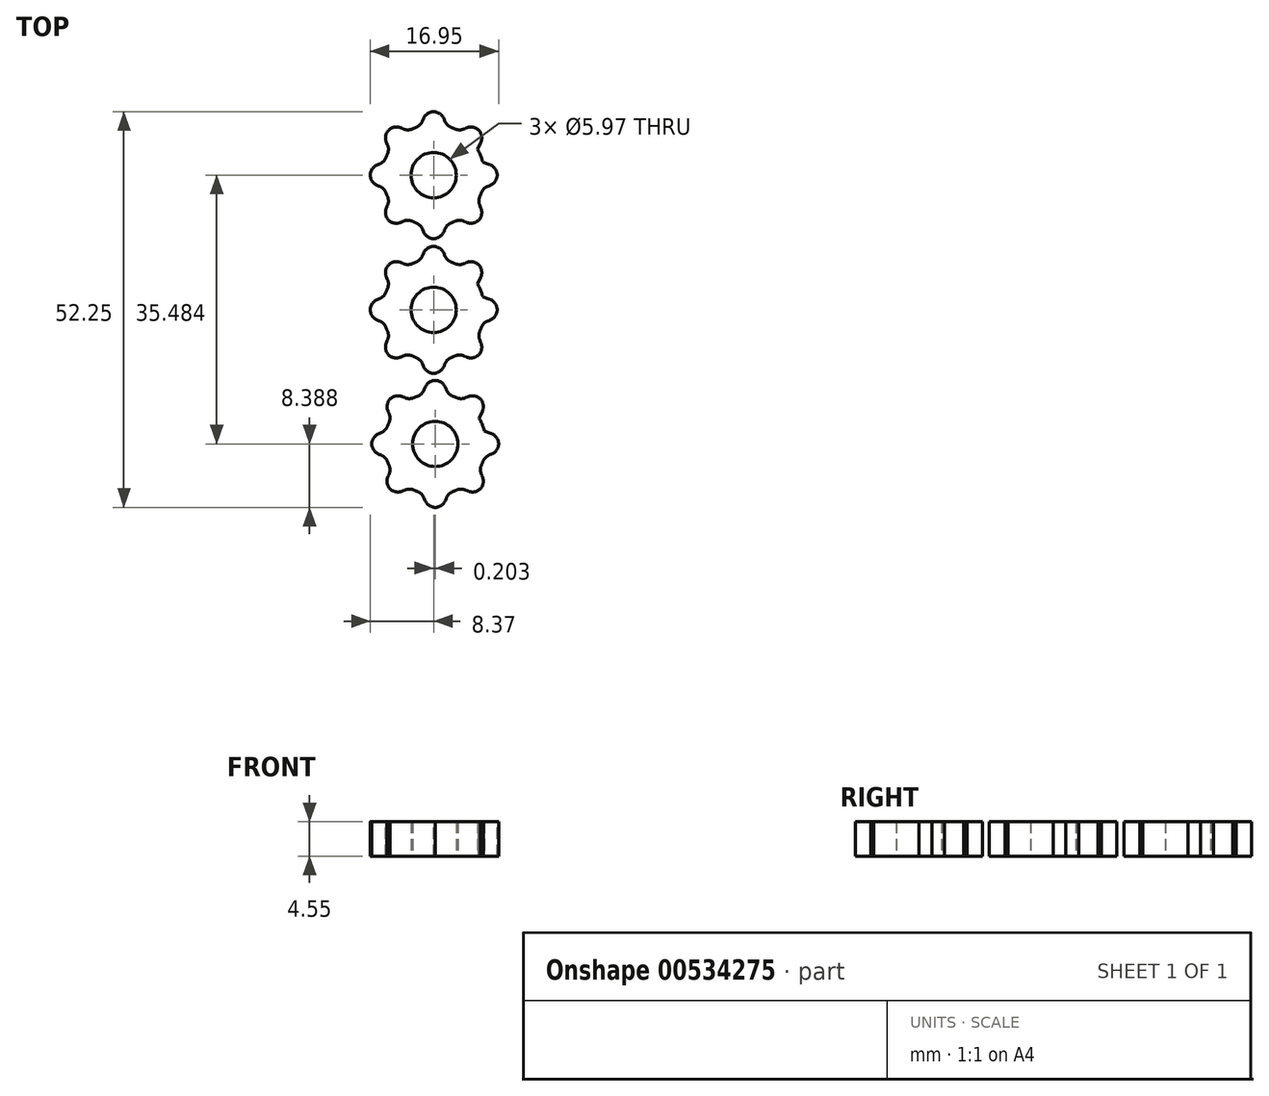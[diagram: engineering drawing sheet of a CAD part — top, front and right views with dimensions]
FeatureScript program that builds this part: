
annotation { "Feature Type Name" : "Feature", "Feature Type Description" : "" }
export const myFeature = defineFeature(function(context is Context, id is Id, definition is map)
    precondition{}
    {
        {
            var Q0;
            Q0=qCreatedBy(makeId("Top.planeOp"),FACE);
            var sketch = newSketch(context, id + "F0", { "sketchPlane" : qUnion([Q0])});
            skCircle(sketch, "E0", {"center": v(-14.29, 61.74) * mm, "radius": 6.71 * mm});
            skLineSegment(sketch, "E1", {"start": v(-22.66, 62.77) * mm, "end": v(-22.66, 60.71) * mm});
            skLineSegment(sketch, "E2", {"start": v(-22.66, 62.77) * mm, "end": v(-20.78, 63.44) * mm});
            skLineSegment(sketch, "E3", {"start": v(-22.66, 60.71) * mm, "end": v(-20.78, 60.04) * mm});
            skLineSegment(sketch, "E4", {"start": v(-19.52, 68.4) * mm, "end": v(-20.95, 66.97) * mm});
            skLineSegment(sketch, "E5", {"start": v(-20.95, 66.97) * mm, "end": v(-20.08, 65.13) * mm});
            skLineSegment(sketch, "E6", {"start": v(-19.52, 68.4) * mm, "end": v(-17.68, 67.54) * mm});
            skLineSegment(sketch, "E7", {"start": v(-15.31, 70.12) * mm, "end": v(-13.27, 70.12) * mm});
            skLineSegment(sketch, "E8", {"start": v(-13.27, 70.12) * mm, "end": v(-12.59, 68.24) * mm});
            skLineSegment(sketch, "E9", {"start": v(-15.31, 70.12) * mm, "end": v(-16, 68.24) * mm});
            skLineSegment(sketch, "E10", {"start": v(-10.9, 67.54) * mm, "end": v(-9.06, 68.4) * mm});
            skLineSegment(sketch, "E11", {"start": v(-9.06, 68.4) * mm, "end": v(-7.63, 66.97) * mm});
            skLineSegment(sketch, "E12", {"start": v(-7.63, 66.97) * mm, "end": v(-8.5, 65.13) * mm});
            skLineSegment(sketch, "E13", {"start": v(-5.9, 62.77) * mm, "end": v(-5.9, 60.72) * mm});
            skLineSegment(sketch, "E14", {"start": v(-5.9, 60.72) * mm, "end": v(-7.8, 60.04) * mm});
            skLineSegment(sketch, "E15", {"start": v(-5.9, 62.77) * mm, "end": v(-7.8, 63.44) * mm});
            skLineSegment(sketch, "E16", {"start": v(-7.63, 56.51) * mm, "end": v(-9.06, 55.08) * mm});
            skLineSegment(sketch, "E17", {"start": v(-9.06, 55.08) * mm, "end": v(-10.9, 55.95) * mm});
            skLineSegment(sketch, "E18", {"start": v(-7.63, 56.51) * mm, "end": v(-8.5, 58.35) * mm});
            skLineSegment(sketch, "E19", {"start": v(-13.27, 53.35) * mm, "end": v(-15.31, 53.35) * mm});
            skLineSegment(sketch, "E20", {"start": v(-15.31, 53.35) * mm, "end": v(-16, 55.25) * mm});
            skLineSegment(sketch, "E21", {"start": v(-13.27, 53.35) * mm, "end": v(-12.59, 55.25) * mm});
            skLineSegment(sketch, "E22", {"start": v(-20.96, 56.5) * mm, "end": v(-19.53, 55.07) * mm});
            skLineSegment(sketch, "E23", {"start": v(-19.53, 55.07) * mm, "end": v(-17.68, 55.95) * mm});
            skLineSegment(sketch, "E24", {"start": v(-20.96, 56.5) * mm, "end": v(-20.08, 58.35) * mm});
            skCircle(sketch, "E25", {"center": v(-14.29, 61.74) * mm, "radius": 2.99 * mm});
            skSolve(sketch);
        }
        {
            var Q0;
            Q0=makeQuery(id+"F0.imprint","IMPRINT",FACE,{"disambiguationData":[TD([[makeQuery(id+"F0.imprint","IMPRINT",EDGE,{"derivedFrom":sQuery(id+"F0.wireOp",EDGE,"E25")}),-1.0]])]});
            extrude(context, id + "F1", {"entities" : qUnion([Q0]), "depth" : 4.55 * mm, "offsetDistance" : 25.4 * mm});
        }
        {
            var Q0;
            Q0=makeQuery(id+"F0.imprint","IMPRINT",FACE,{"disambiguationData":[TD([[makeQuery(id+"F0.imprint","IMPRINT",EDGE,{"derivedFrom":sQuery(id+"F0.wireOp",EDGE,"E1")}),1.0]])]});
            var Q1;
            Q1=makeQuery(id+"F0.imprint","IMPRINT",FACE,{"disambiguationData":[TD([[makeQuery(id+"F0.imprint","IMPRINT",EDGE,{"derivedFrom":sQuery(id+"F0.wireOp",EDGE,"E7")}),-1.0]])]});
            var Q2;
            Q2=makeQuery(id+"F0.imprint","IMPRINT",FACE,{"disambiguationData":[TD([[makeQuery(id+"F0.imprint","IMPRINT",EDGE,{"derivedFrom":sQuery(id+"F0.wireOp",EDGE,"E4")}),1.0]])]});
            var Q3;
            {var subQ0=sQuery(id+"F0.wireOp",EDGE,"E10");Q3=makeQuery(id+"F0.imprint","IMPRINT",FACE,{"disambiguationData":[TD([[makeQuery(id+"F0.imprint","IMPRINT",EDGE,{"derivedFrom":subQ0}),-1.0]])]});}
            var Q4;
            Q4=makeQuery(id+"F0.imprint","IMPRINT",FACE,{"disambiguationData":[TD([[makeQuery(id+"F0.imprint","IMPRINT",EDGE,{"derivedFrom":sQuery(id+"F0.wireOp",EDGE,"E13")}),-1.0]])]});
            var Q5;
            Q5=makeQuery(id+"F0.imprint","IMPRINT",FACE,{"disambiguationData":[TD([[makeQuery(id+"F0.imprint","IMPRINT",EDGE,{"derivedFrom":sQuery(id+"F0.wireOp",EDGE,"E16")}),-1.0]])]});
            var Q6;
            Q6=makeQuery(id+"F0.imprint","IMPRINT",FACE,{"disambiguationData":[TD([[makeQuery(id+"F0.imprint","IMPRINT",EDGE,{"derivedFrom":sQuery(id+"F0.wireOp",EDGE,"E19")}),-1.0]])]});
            var Q7;
            Q7=makeQuery(id+"F0.imprint","IMPRINT",FACE,{"disambiguationData":[TD([[makeQuery(id+"F0.imprint","IMPRINT",EDGE,{"derivedFrom":sQuery(id+"F0.wireOp",EDGE,"E22")}),1.0]])]});
            extrude(context, id + "F2", {"entities" : qUnion([Q0, Q1, Q2, Q3, Q4, Q5, Q6, Q7]), "operationType" : NewBodyOperationType.ADD, "depth" : 4.55 * mm, "offsetDistance" : 25.4 * mm});
        }
        {
            var Q0;
            Q0=makeQuery(id+"F2.opExtrude","SWEPT_EDGE",EDGE,{"disambiguationData":[OSD([sQuery(id+"F0.wireOp",EDGE,"E13"),sQuery(id+"F0.wireOp",EDGE,"E15")])]});
            var Q1;
            Q1=makeQuery(id+"F2.opExtrude","SWEPT_EDGE",EDGE,{"disambiguationData":[OSD([sQuery(id+"F0.wireOp",EDGE,"E13"),sQuery(id+"F0.wireOp",EDGE,"E14")])]});
            var Q2;
            Q2=makeQuery(id+"F2.opExtrude","SWEPT_EDGE",EDGE,{"disambiguationData":[OSD([sQuery(id+"F0.wireOp",EDGE,"E16"),sQuery(id+"F0.wireOp",EDGE,"E18")])]});
            var Q3;
            Q3=makeQuery(id+"F2.opExtrude","SWEPT_EDGE",EDGE,{"disambiguationData":[OSD([sQuery(id+"F0.wireOp",EDGE,"E16"),sQuery(id+"F0.wireOp",EDGE,"E17")])]});
            var Q4;
            Q4=makeQuery(id+"F2.opExtrude","SWEPT_EDGE",EDGE,{"disambiguationData":[OSD([sQuery(id+"F0.wireOp",EDGE,"E19"),sQuery(id+"F0.wireOp",EDGE,"E21")])]});
            var Q5;
            Q5=makeQuery(id+"F2.opExtrude","SWEPT_EDGE",EDGE,{"disambiguationData":[OSD([sQuery(id+"F0.wireOp",EDGE,"E19"),sQuery(id+"F0.wireOp",EDGE,"E20")])]});
            var Q6;
            Q6=makeQuery(id+"F2.opExtrude","SWEPT_EDGE",EDGE,{"disambiguationData":[OSD([sQuery(id+"F0.wireOp",EDGE,"E22"),sQuery(id+"F0.wireOp",EDGE,"E23")])]});
            var Q7;
            Q7=makeQuery(id+"F2.opExtrude","SWEPT_EDGE",EDGE,{"disambiguationData":[OSD([sQuery(id+"F0.wireOp",EDGE,"E22"),sQuery(id+"F0.wireOp",EDGE,"E24")])]});
            var Q8;
            Q8=makeQuery(id+"F2.opExtrude","SWEPT_EDGE",EDGE,{"disambiguationData":[OSD([sQuery(id+"F0.wireOp",EDGE,"E1"),sQuery(id+"F0.wireOp",EDGE,"E3")])]});
            var Q9;
            Q9=makeQuery(id+"F2.opExtrude","SWEPT_EDGE",EDGE,{"disambiguationData":[OSD([sQuery(id+"F0.wireOp",EDGE,"E1"),sQuery(id+"F0.wireOp",EDGE,"E2")])]});
            var Q10;
            Q10=makeQuery(id+"F2.opExtrude","SWEPT_EDGE",EDGE,{"disambiguationData":[OSD([sQuery(id+"F0.wireOp",EDGE,"E4"),sQuery(id+"F0.wireOp",EDGE,"E5")])]});
            var Q11;
            Q11=makeQuery(id+"F2.opExtrude","SWEPT_EDGE",EDGE,{"disambiguationData":[OSD([sQuery(id+"F0.wireOp",EDGE,"E4"),sQuery(id+"F0.wireOp",EDGE,"E6")])]});
            var Q12;
            Q12=makeQuery(id+"F2.opExtrude","SWEPT_EDGE",EDGE,{"disambiguationData":[OSD([sQuery(id+"F0.wireOp",EDGE,"E7"),sQuery(id+"F0.wireOp",EDGE,"E9")])]});
            var Q13;
            Q13=makeQuery(id+"F2.opExtrude","SWEPT_EDGE",EDGE,{"disambiguationData":[OSD([sQuery(id+"F0.wireOp",EDGE,"E7"),sQuery(id+"F0.wireOp",EDGE,"E8")])]});
            var Q14;
            Q14=makeQuery(id+"F2.opExtrude","SWEPT_EDGE",EDGE,{"disambiguationData":[OSD([sQuery(id+"F0.wireOp",EDGE,"E10"),sQuery(id+"F0.wireOp",EDGE,"E11")])]});
            var Q15;
            Q15=makeQuery(id+"F2.opExtrude","SWEPT_EDGE",EDGE,{"disambiguationData":[OSD([sQuery(id+"F0.wireOp",EDGE,"E11"),sQuery(id+"F0.wireOp",EDGE,"E12")])]});
            var Q16;
            Q16=makeQuery(id+"F2.opExtrude","SWEPT_EDGE",EDGE,{"disambiguationData":[OSD([sQuery(id+"F0.wireOp",EDGE,"E0"),sQuery(id+"F0.wireOp",EDGE,"E8")])]});
            var Q17;
            Q17=makeQuery(id+"F2.opExtrude","SWEPT_EDGE",EDGE,{"disambiguationData":[OSD([sQuery(id+"F0.wireOp",EDGE,"E0"),sQuery(id+"F0.wireOp",EDGE,"E10")])]});
            var Q18;
            Q18=makeQuery(id+"F2.opExtrude","SWEPT_EDGE",EDGE,{"disambiguationData":[OSD([sQuery(id+"F0.wireOp",EDGE,"E0"),sQuery(id+"F0.wireOp",EDGE,"E12")])]});
            var Q19;
            Q19=makeQuery(id+"F2.opExtrude","SWEPT_EDGE",EDGE,{"disambiguationData":[OSD([sQuery(id+"F0.wireOp",EDGE,"E0"),sQuery(id+"F0.wireOp",EDGE,"E15")])]});
            var Q20;
            Q20=makeQuery(id+"F2.opExtrude","SWEPT_EDGE",EDGE,{"disambiguationData":[OSD([sQuery(id+"F0.wireOp",EDGE,"E0"),sQuery(id+"F0.wireOp",EDGE,"E14")])]});
            var Q21;
            Q21=makeQuery(id+"F2.opExtrude","SWEPT_EDGE",EDGE,{"disambiguationData":[OSD([sQuery(id+"F0.wireOp",EDGE,"E0"),sQuery(id+"F0.wireOp",EDGE,"E18")])]});
            var Q22;
            Q22=makeQuery(id+"F2.opExtrude","SWEPT_EDGE",EDGE,{"disambiguationData":[OSD([sQuery(id+"F0.wireOp",EDGE,"E0"),sQuery(id+"F0.wireOp",EDGE,"E17")])]});
            var Q23;
            Q23=makeQuery(id+"F2.opExtrude","SWEPT_EDGE",EDGE,{"disambiguationData":[OSD([sQuery(id+"F0.wireOp",EDGE,"E0"),sQuery(id+"F0.wireOp",EDGE,"E21")])]});
            var Q24;
            Q24=makeQuery(id+"F2.opExtrude","SWEPT_EDGE",EDGE,{"disambiguationData":[OSD([sQuery(id+"F0.wireOp",EDGE,"E0"),sQuery(id+"F0.wireOp",EDGE,"E20")])]});
            var Q25;
            Q25=makeQuery(id+"F2.opExtrude","SWEPT_EDGE",EDGE,{"disambiguationData":[OSD([sQuery(id+"F0.wireOp",EDGE,"E0"),sQuery(id+"F0.wireOp",EDGE,"E23")])]});
            var Q26;
            Q26=makeQuery(id+"F2.opExtrude","SWEPT_EDGE",EDGE,{"disambiguationData":[OSD([sQuery(id+"F0.wireOp",EDGE,"E0"),sQuery(id+"F0.wireOp",EDGE,"E3")])]});
            var Q27;
            Q27=makeQuery(id+"F2.opExtrude","SWEPT_EDGE",EDGE,{"disambiguationData":[OSD([sQuery(id+"F0.wireOp",EDGE,"E0"),sQuery(id+"F0.wireOp",EDGE,"E24")])]});
            var Q28;
            Q28=makeQuery(id+"F2.opExtrude","SWEPT_EDGE",EDGE,{"disambiguationData":[OSD([sQuery(id+"F0.wireOp",EDGE,"E0"),sQuery(id+"F0.wireOp",EDGE,"E2")])]});
            var Q29;
            Q29=makeQuery(id+"F2.opExtrude","SWEPT_EDGE",EDGE,{"disambiguationData":[OSD([sQuery(id+"F0.wireOp",EDGE,"E0"),sQuery(id+"F0.wireOp",EDGE,"E6")])]});
            var Q30;
            Q30=makeQuery(id+"F2.opExtrude","SWEPT_EDGE",EDGE,{"disambiguationData":[OSD([sQuery(id+"F0.wireOp",EDGE,"E0"),sQuery(id+"F0.wireOp",EDGE,"E9")])]});
            var Q31;
            Q31=makeQuery(id+"F2.opExtrude","SWEPT_EDGE",EDGE,{"disambiguationData":[OSD([sQuery(id+"F0.wireOp",EDGE,"E0"),sQuery(id+"F0.wireOp",EDGE,"E5")])]});
            fillet(context, id + "F3", {"entities" : qUnion([Q0, Q1, Q2, Q3, Q4, Q5, Q6, Q7, Q8, Q9, Q10, Q11, Q12, Q13, Q14, Q15, Q16, Q17, Q18, Q19, Q20, Q21, Q22, Q23, Q24, Q25, Q26, Q27, Q28, Q29, Q30, Q31]), "radius" : 1.52 * mm, "tangentPropagation" : true, "allowEdgeOverflow" : false});
        }
        {
            var Q0;
            Q0=makeQuery(id+"F1.opExtrude","SWEPT_BODY",BODY,{"disambiguationData":[OSD([sQuery(id+"F0.wireOp",EDGE,"E0"),sQuery(id+"F0.wireOp",EDGE,"E25")])]});
            transform(context, id + "F4", {"entities" : qUnion([Q0]), "transformType" : TransformType.TRANSLATION_3D, "dx" : 0 * mm, "dy" : -17.78 * mm, "dz" : 0 * mm, "makeCopy" : true});
        }
        {
            var Q0;
            Q0=makeQuery(id+"F4.opPattern","COPY",BODY,{"derivedFrom":makeQuery(id+"F1.opExtrude","SWEPT_BODY",BODY,{"disambiguationData":[OSD([sQuery(id+"F0.wireOp",EDGE,"E0"),sQuery(id+"F0.wireOp",EDGE,"E25")])]}),"instanceName":"1"});
            transform(context, id + "F5", {"entities" : qUnion([Q0]), "transformType" : TransformType.TRANSLATION_3D, "dx" : 0.2 * mm, "dy" : -17.7 * mm, "dz" : 0 * mm, "makeCopy" : true});
        }
    });
